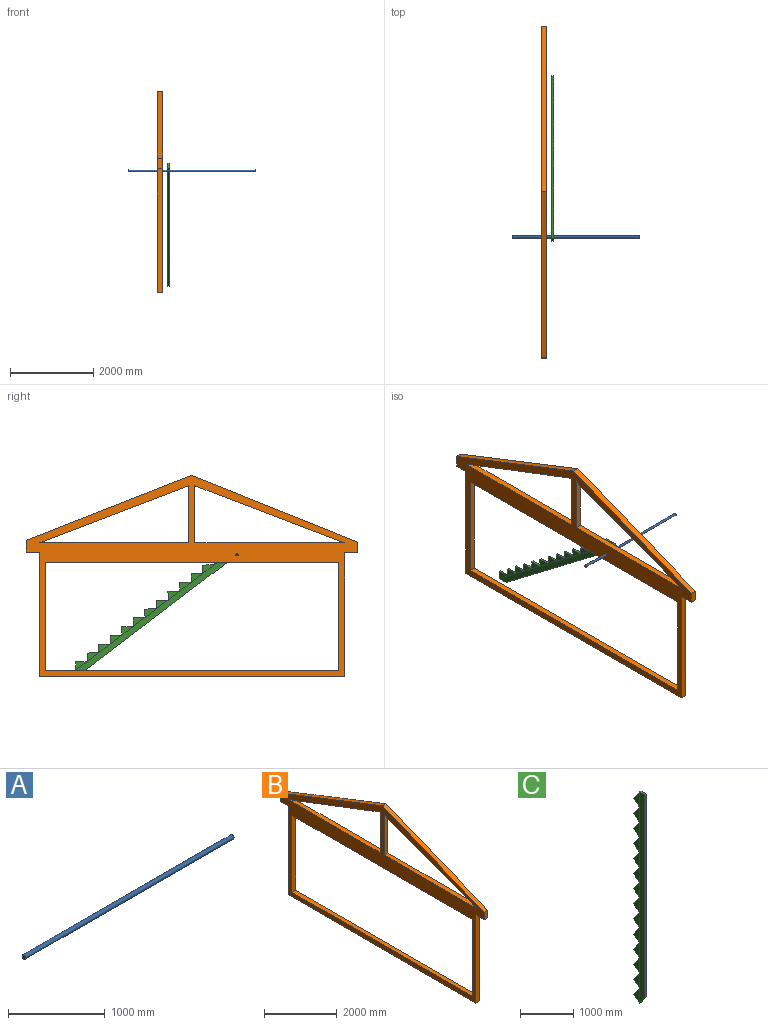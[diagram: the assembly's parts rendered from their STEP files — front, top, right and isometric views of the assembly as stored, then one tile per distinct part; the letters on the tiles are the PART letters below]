
ASSEMBLY  parts=3 mates=2
PART A: 3 faces, bbox 3048x50.8x50.8 mm
  f0: cylinder r=25.4mm len=3048mm, axis (-1,0,0), area 486439.2mm2, adj f1,f2
  f1: plane 50.8x50.8mm, normal (1,0,0), area 2026.8mm2, adj f0
  f2: plane 50.8x50.8mm, normal (-1,0,0), area 2026.8mm2, adj f0
PART B: 22 faces, bbox 139.7x7953.2x4825.2 mm
  f0: plane 258.16x139.7mm, normal (0,-1,0), area 36065.6mm2, adj f1,f18,f19,f20
  f1: plane 322.76x139.7mm, normal (0,0,-1), area 45089.9mm2, adj f0,f2,f19,f20
  f2: plane 2967.81x139.7mm, normal (0,-1,0), area 414602.5mm2, adj f1,f3,f19,f20
  f3: plane 7318.53x139.7mm, normal (0,0,-1), area 1022398.8mm2, adj f2,f4,f19,f20
  f4: plane 2985.72x139.7mm, normal (0,1,0), area 417105.6mm2, adj f3,f5,f19,f20
  f5: plane 311.93x139.7mm, normal (0,0,-1), area 43576.8mm2, adj f4,f6,f19,f20
  f6: plane 282x139.7mm, normal (0,1,0), area 39394.7mm2, adj f5,f7,f19,f20
  f7: plane 3970.59x1557.48mm, normal (0,0.37,0.93), area 595838.2mm2, adj f6,f18,f19,f20
  f8: plane 1368.16x139.7mm, normal (0,1,0), area 191132.3mm2, adj f9,f15,f19,f20
  f9: plane 3580.78x1368.16mm, normal (0,-0.36,-0.93), area 535506.5mm2, adj f8,f15,f19,f20
  f10: plane 2593.16x139.7mm, normal (0,1,0), area 362264.1mm2, adj f11,f16,f19,f20
  f11: plane 7028.27x139.7mm, normal (0,0,-1), area 981849.8mm2, adj f10,f12,f19,f20
  f12: plane 2593.16x139.7mm, normal (0,-1,0), area 362264.1mm2, adj f11,f16,f19,f20
  f13: plane 3583.01x139.7mm, normal (0,0,1), area 500546.5mm2, adj f14,f17,f19,f20
  f14: plane 3583.01x1368.16mm, normal (0,0.36,-0.93), area 535796.9mm2, adj f13,f17,f19,f20
  f15: plane 3580.78x139.7mm, normal (0,0,1), area 500235.6mm2, adj f8,f9,f19,f20
  f16: plane 7028.27x139.7mm, normal (0,0,1), area 981849.8mm2, adj f10,f12,f19,f20
  f17: plane 1368.16x139.7mm, normal (0,-1,0), area 191132.3mm2, adj f13,f14,f19,f20
  f18: plane 3982.64x1599.23mm, normal (0,-0.37,0.93), area 599554.9mm2, adj f0,f7,f19,f20
  f19: plane 7953.22x4825.2mm, normal (1,0,0), area 7082622.7mm2, adj f0,f1,f2,f3,f4,f5,f6,f7
  f20: plane 7953.22x4825.2mm, normal (-1,0,0), area 7082622.7mm2, adj f0,f1,f2,f3,f4,f5,f6,f7
  f21: cylinder r=20.96mm len=139.7mm, axis (1,0,0), area 18400.2mm2, adj f19,f20
PART C: 81 faces, bbox 44.5x303.9x4876.8 mm
  f0: plane 4533.06x43.69mm, normal (0,-1,0), area 198040.5mm2, adj f1,f2,f77,f79
  f1: plane 4876.8x139.7mm, normal (-1,0,0), area 667438.9mm2, adj f0,f3,f4,f5,f6,f7,f8,f9
  f2: plane 4876.8x303.93mm, normal (1,0,0), area 1064458.5mm2, adj f0,f3,f4,f5,f6,f7,f8,f9
  f3: plane 43.69x2.62mm, normal (0,1,0), area 114.6mm2, adj f1,f2,f71,f74
  f4: plane 43.69x2.62mm, normal (0,1,0), area 114.6mm2, adj f1,f2,f67,f70
  f5: plane 43.69x2.62mm, normal (0,1,0), area 114.6mm2, adj f1,f2,f63,f66
  f6: plane 43.69x2.62mm, normal (0,1,0), area 114.6mm2, adj f1,f2,f59,f62
  f7: plane 43.69x2.62mm, normal (0,1,0), area 114.6mm2, adj f1,f2,f55,f58
  f8: plane 43.69x2.62mm, normal (0,1,0), area 114.6mm2, adj f1,f2,f51,f54
  f9: plane 43.69x2.62mm, normal (0,1,0), area 114.6mm2, adj f1,f2,f47,f50
  f10: plane 43.69x2.62mm, normal (0,1,0), area 114.6mm2, adj f1,f2,f43,f46
  f11: plane 43.69x2.62mm, normal (0,1,0), area 114.6mm2, adj f1,f2,f39,f42
  f12: plane 43.69x2.62mm, normal (0,1,0), area 114.6mm2, adj f1,f2,f35,f38
  f13: plane 43.69x2.62mm, normal (0,1,0), area 114.6mm2, adj f1,f2,f31,f34
  f14: plane 43.69x2.62mm, normal (0,1,0), area 114.6mm2, adj f1,f2,f27,f30
  f15: plane 43.69x2.62mm, normal (0,1,0), area 114.6mm2, adj f1,f2,f22,f26
  f16: plane 43.69x0.35mm, normal (0,1,0), area 15.1mm2, adj f1,f2,f20,f23
  f17: plane 127x43.69mm, normal (0,-1,0), area 5548.4mm2, adj f1,f2,f19,f78
  f18: plane 43.69x7.36mm, normal (0,1,0), area 321.4mm2, adj f1,f2,f19,f75
  f19: plane 139.7x43.69mm, normal (0,0,1), area 6103.2mm2, adj f1,f2,f17,f18
  f20: plane 43.69x0mm, normal (0,0,-1), area 0.1mm2, adj f1,f2,f16,f77
  f21: plane 345.36x0.76mm, normal (0,-1,0), area 263.2mm2, adj f1,f22,f23,f24
  f22: plane 226.04x164.23mm, normal (0,0.81,0.59), area 12419.3mm2, adj f2,f15,f21,f23,f24
  f23: plane 164.23x119.32mm, normal (0,0.59,-0.81), area 9023.2mm2, adj f2,f16,f21,f22,f24
  f24: plane 345.36x164.23mm, normal (-1,0,0), area 28358.5mm2, adj f21,f22,f23
  f25: plane 345.36x0.76mm, normal (0,-1,0), area 263.2mm2, adj f1,f26,f27,f28
  f26: plane 164.23x119.32mm, normal (0,0.59,-0.81), area 9023.2mm2, adj f2,f15,f25,f27,f28
  f27: plane 226.04x164.23mm, normal (0,0.81,0.59), area 12419.3mm2, adj f2,f14,f25,f26,f28
  f28: plane 345.36x164.23mm, normal (-1,0,0), area 28358.5mm2, adj f25,f26,f27
  f29: plane 345.36x0.76mm, normal (0,-1,0), area 263.2mm2, adj f1,f30,f31,f32
  f30: plane 164.23x119.32mm, normal (0,0.59,-0.81), area 9023.2mm2, adj f2,f14,f29,f31,f32
  f31: plane 226.04x164.23mm, normal (0,0.81,0.59), area 12419.3mm2, adj f2,f13,f29,f30,f32
  f32: plane 345.36x164.23mm, normal (-1,0,0), area 28358.5mm2, adj f29,f30,f31
  f33: plane 345.36x0.76mm, normal (0,-1,0), area 263.2mm2, adj f1,f34,f35,f36
  f34: plane 164.23x119.32mm, normal (0,0.59,-0.81), area 9023.2mm2, adj f2,f13,f33,f35,f36
  f35: plane 226.04x164.23mm, normal (0,0.81,0.59), area 12419.3mm2, adj f2,f12,f33,f34,f36
  f36: plane 345.36x164.23mm, normal (-1,0,0), area 28358.5mm2, adj f33,f34,f35
  f37: plane 345.36x0.76mm, normal (0,-1,0), area 263.2mm2, adj f1,f38,f39,f40
  f38: plane 164.23x119.32mm, normal (0,0.59,-0.81), area 9023.2mm2, adj f2,f12,f37,f39,f40
  f39: plane 226.04x164.23mm, normal (0,0.81,0.59), area 12419.3mm2, adj f2,f11,f37,f38,f40
  f40: plane 345.36x164.23mm, normal (-1,0,0), area 28358.5mm2, adj f37,f38,f39
  f41: plane 345.36x0.76mm, normal (0,-1,0), area 263.2mm2, adj f1,f42,f43,f44
  f42: plane 164.23x119.32mm, normal (0,0.59,-0.81), area 9023.2mm2, adj f2,f11,f41,f43,f44
  f43: plane 226.04x164.23mm, normal (0,0.81,0.59), area 12419.3mm2, adj f2,f10,f41,f42,f44
  f44: plane 345.36x164.23mm, normal (-1,0,0), area 28358.5mm2, adj f41,f42,f43
  f45: plane 345.36x0.76mm, normal (0,-1,0), area 263.2mm2, adj f1,f46,f47,f48
  f46: plane 164.23x119.32mm, normal (0,0.59,-0.81), area 9023.2mm2, adj f2,f10,f45,f47,f48
  f47: plane 226.04x164.23mm, normal (0,0.81,0.59), area 12419.3mm2, adj f2,f9,f45,f46,f48
  f48: plane 345.36x164.23mm, normal (-1,0,0), area 28358.5mm2, adj f45,f46,f47
  f49: plane 345.36x0.76mm, normal (0,-1,0), area 263.2mm2, adj f1,f50,f51,f52
  f50: plane 164.23x119.32mm, normal (0,0.59,-0.81), area 9023.2mm2, adj f2,f9,f49,f51,f52
  f51: plane 226.04x164.23mm, normal (0,0.81,0.59), area 12419.3mm2, adj f2,f8,f49,f50,f52
  f52: plane 345.36x164.23mm, normal (-1,0,0), area 28358.5mm2, adj f49,f50,f51
  f53: plane 345.36x0.76mm, normal (0,-1,0), area 263.2mm2, adj f1,f54,f55,f56
  f54: plane 164.23x119.32mm, normal (0,0.59,-0.81), area 9023.2mm2, adj f2,f8,f53,f55,f56
  f55: plane 226.04x164.23mm, normal (0,0.81,0.59), area 12419.3mm2, adj f2,f7,f53,f54,f56
  f56: plane 345.36x164.23mm, normal (-1,0,0), area 28358.5mm2, adj f53,f54,f55
  f57: plane 345.36x0.76mm, normal (0,-1,0), area 263.2mm2, adj f1,f58,f59,f60
  f58: plane 164.23x119.32mm, normal (0,0.59,-0.81), area 9023.2mm2, adj f2,f7,f57,f59,f60
  f59: plane 226.04x164.23mm, normal (0,0.81,0.59), area 12419.3mm2, adj f2,f6,f57,f58,f60
  f60: plane 345.36x164.23mm, normal (-1,0,0), area 28358.5mm2, adj f57,f58,f59
  f61: plane 345.36x0.76mm, normal (0,-1,0), area 263.2mm2, adj f1,f62,f63,f64
  f62: plane 164.23x119.32mm, normal (0,0.59,-0.81), area 9023.2mm2, adj f2,f6,f61,f63,f64
  f63: plane 226.04x164.23mm, normal (0,0.81,0.59), area 12419.3mm2, adj f2,f5,f61,f62,f64
  f64: plane 345.36x164.23mm, normal (-1,0,0), area 28358.5mm2, adj f61,f62,f63
  f65: plane 345.36x0.76mm, normal (0,-1,0), area 263.2mm2, adj f1,f66,f67,f68
  f66: plane 164.23x119.32mm, normal (0,0.59,-0.81), area 9023.2mm2, adj f2,f5,f65,f67,f68
  f67: plane 226.04x164.23mm, normal (0,0.81,0.59), area 12419.3mm2, adj f2,f4,f65,f66,f68
  f68: plane 345.36x164.23mm, normal (-1,0,0), area 28358.5mm2, adj f65,f66,f67
  f69: plane 345.36x0.76mm, normal (0,-1,0), area 263.2mm2, adj f1,f70,f71,f72
  f70: plane 164.23x119.32mm, normal (0,0.59,-0.81), area 9023.2mm2, adj f2,f4,f69,f71,f72
  f71: plane 226.04x164.23mm, normal (0,0.81,0.59), area 12419.3mm2, adj f2,f3,f69,f70,f72
  f72: plane 345.36x164.23mm, normal (-1,0,0), area 28358.5mm2, adj f69,f70,f71
  f73: plane 345.36x0.76mm, normal (0,-1,0), area 263.2mm2, adj f1,f74,f75,f76
  f74: plane 164.23x119.32mm, normal (0,0.59,-0.81), area 9023.2mm2, adj f2,f3,f73,f75,f76
  f75: plane 226.04x164.23mm, normal (0,0.81,0.59), area 12419.3mm2, adj f2,f18,f73,f74,f76
  f76: plane 345.36x164.23mm, normal (-1,0,0), area 28358.5mm2, adj f73,f74,f75
  f77: plane 190.36x139.7mm, normal (0,-0.81,-0.59), area 10315.6mm2, adj f0,f1,f2,f20
  f78: plane 43.69x20.99mm, normal (0,0,-1), area 916.8mm2, adj f1,f2,f17,f80
  f79: plane 43.69x20.99mm, normal (0,0,1), area 916.8mm2, adj f0,f1,f2,f80
  f80: plane 43.69x26.38mm, normal (0,-1,0), area 1152.3mm2, adj f1,f2,f78,f79
PLACE A t=(39.24,-555.72,1053.49)mm
PLACE B t=(727.16,-459.18,1077.13)mm
PLACE C rot(axis=(1,0,0),52.7deg) t=(1548,3095.59,-2440.02)mm
MATE cylindrical C.f2 <-> A.f0  axis (1,0,0) through (4801.66,1832.14,3995.34)mm
MATE cylindrical B.f21 <-> C.f2  axis (1,0,0) through (4642.88,1832.14,3995.34)mm
